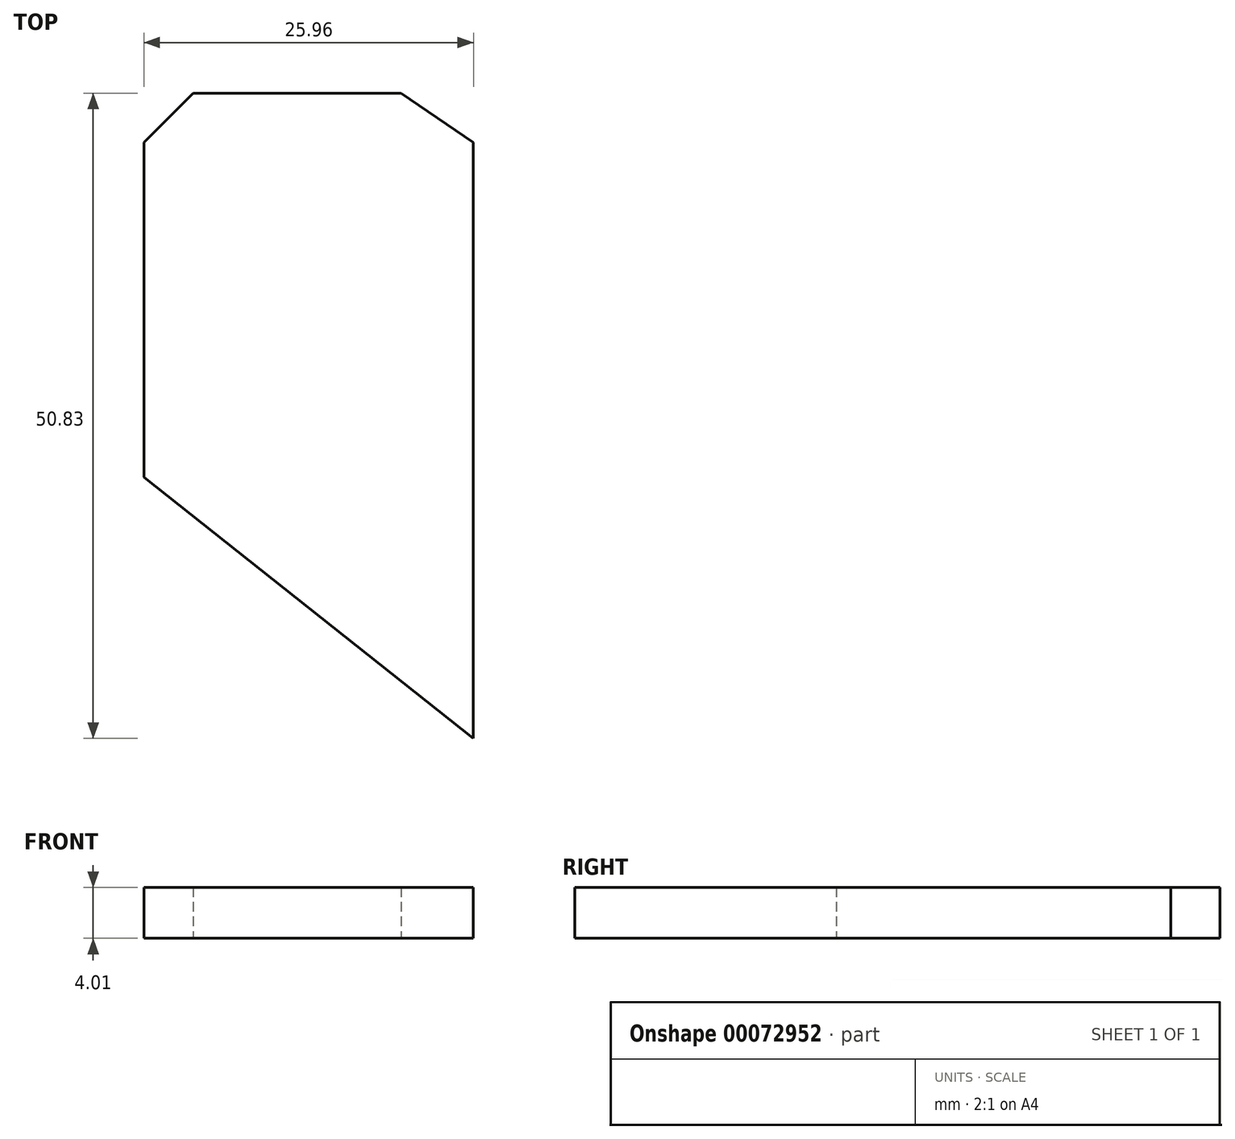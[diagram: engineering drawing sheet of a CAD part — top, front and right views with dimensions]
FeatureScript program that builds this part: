
annotation { "Feature Type Name" : "Feature", "Feature Type Description" : "" }
export const myFeature = defineFeature(function(context is Context, id is Id, definition is map)
    precondition{}
    {
        {
            var Q0;
            Q0=qCreatedBy(makeId("Top.planeOp"),FACE);
            var sketch = newSketch(context, id + "F0", { "sketchPlane" : qUnion([Q0])});
            skLineSegment(sketch, "E0", {"start": v(-37.55, 26.37) * mm, "end": v(-37.55, 0) * mm});
            skLineSegment(sketch, "E1", {"start": v(-37.55, 0) * mm, "end": v(-11.6, -20.58) * mm});
            skLineSegment(sketch, "E2", {"start": v(-11.6, -20.58) * mm, "end": v(-11.6, 0) * mm});
            skLineSegment(sketch, "E3", {"start": v(-11.6, 0) * mm, "end": v(-11.6, 26.37) * mm});
            skLineSegment(sketch, "E4", {"start": v(-11.6, 26.37) * mm, "end": v(-17.28, 30.25) * mm});
            skLineSegment(sketch, "E5", {"start": v(-17.28, 30.25) * mm, "end": v(-33.67, 30.25) * mm});
            skLineSegment(sketch, "E6", {"start": v(-33.67, 30.25) * mm, "end": v(-37.55, 26.37) * mm});
            skSolve(sketch);
        }
        {
            var Q0;
            Q0=makeQuery(id+"F0.imprint","IMPRINT",FACE,{"disambiguationData":[TD([[makeQuery(id+"F0.imprint","IMPRINT",EDGE,{"derivedFrom":sQuery(id+"F0.wireOp",EDGE,"E0")}),1.0]])]});
            extrude(context, id + "F1", {"entities" : qUnion([Q0]), "depth" : 4 * mm});
        }
    });
